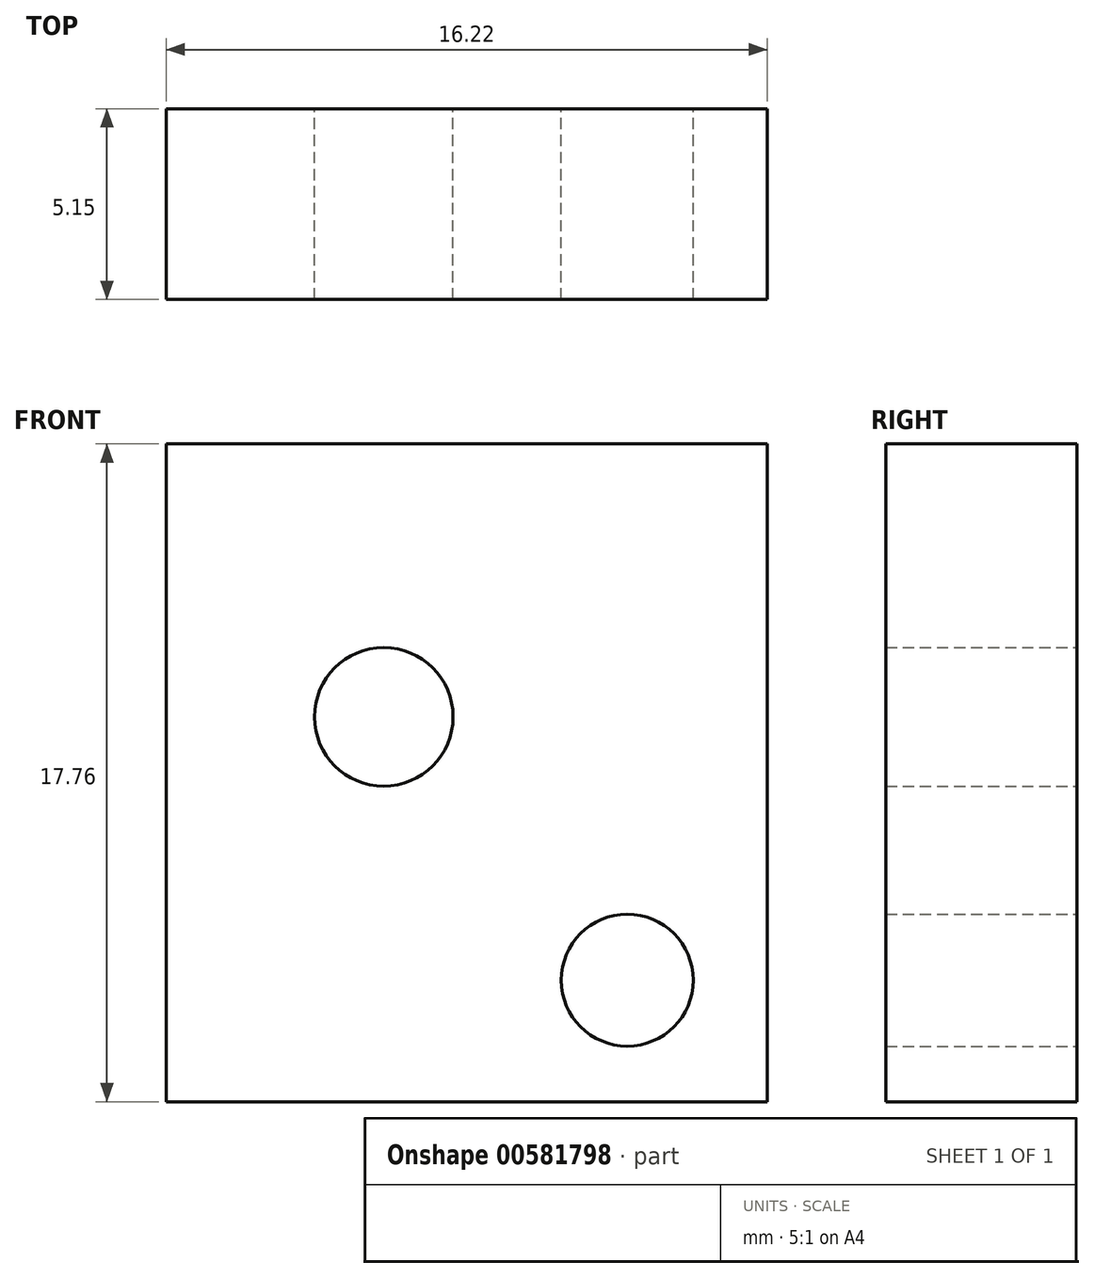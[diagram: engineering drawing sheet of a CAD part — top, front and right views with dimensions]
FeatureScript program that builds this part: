
annotation { "Feature Type Name" : "Feature", "Feature Type Description" : "" }
export const myFeature = defineFeature(function(context is Context, id is Id, definition is map)
    precondition{}
    {
        {
            var Q0;
            Q0=qCreatedBy(makeId("Front.planeOp"),FACE);
            var sketch = newSketch(context, id + "F0", { "sketchPlane" : qUnion([Q0])});
            skLineSegment(sketch, "E0.bottom", {"start": v(8.1, 8.88) * mm, "end": v(-8.11, 8.88) * mm});
            skLineSegment(sketch, "E0.top", {"start": v(8.1, -8.88) * mm, "end": v(-8.11, -8.88) * mm});
            skLineSegment(sketch, "E0.left", {"start": v(8.1, 8.88) * mm, "end": v(8.1, -8.88) * mm});
            skLineSegment(sketch, "E0.right", {"start": v(-8.11, 8.88) * mm, "end": v(-8.11, -8.88) * mm});
            skPoint(sketch, "E0.middle", {"position": v(0, 0) * mm});
            skCircle(sketch, "E1", {"center": v(-2.24, 1.51) * mm, "radius": 1.87 * mm});
            skCircle(sketch, "E2", {"center": v(4.33, -5.6) * mm, "radius": 1.78 * mm});
            skSolve(sketch);
        }
        {
            var Q0;
            Q0=makeQuery(id+"F0.imprint","IMPRINT",FACE,{"disambiguationData":[TD([[makeQuery(id+"F0.imprint","IMPRINT",EDGE,{"derivedFrom":sQuery(id+"F0.wireOp",EDGE,"E0.bottom")}),1.0]])]});
            extrude(context, id + "F1", {"entities" : qUnion([Q0]), "depth" : 5.15 * mm, "offsetDistance" : 25 * mm});
        }
    });
